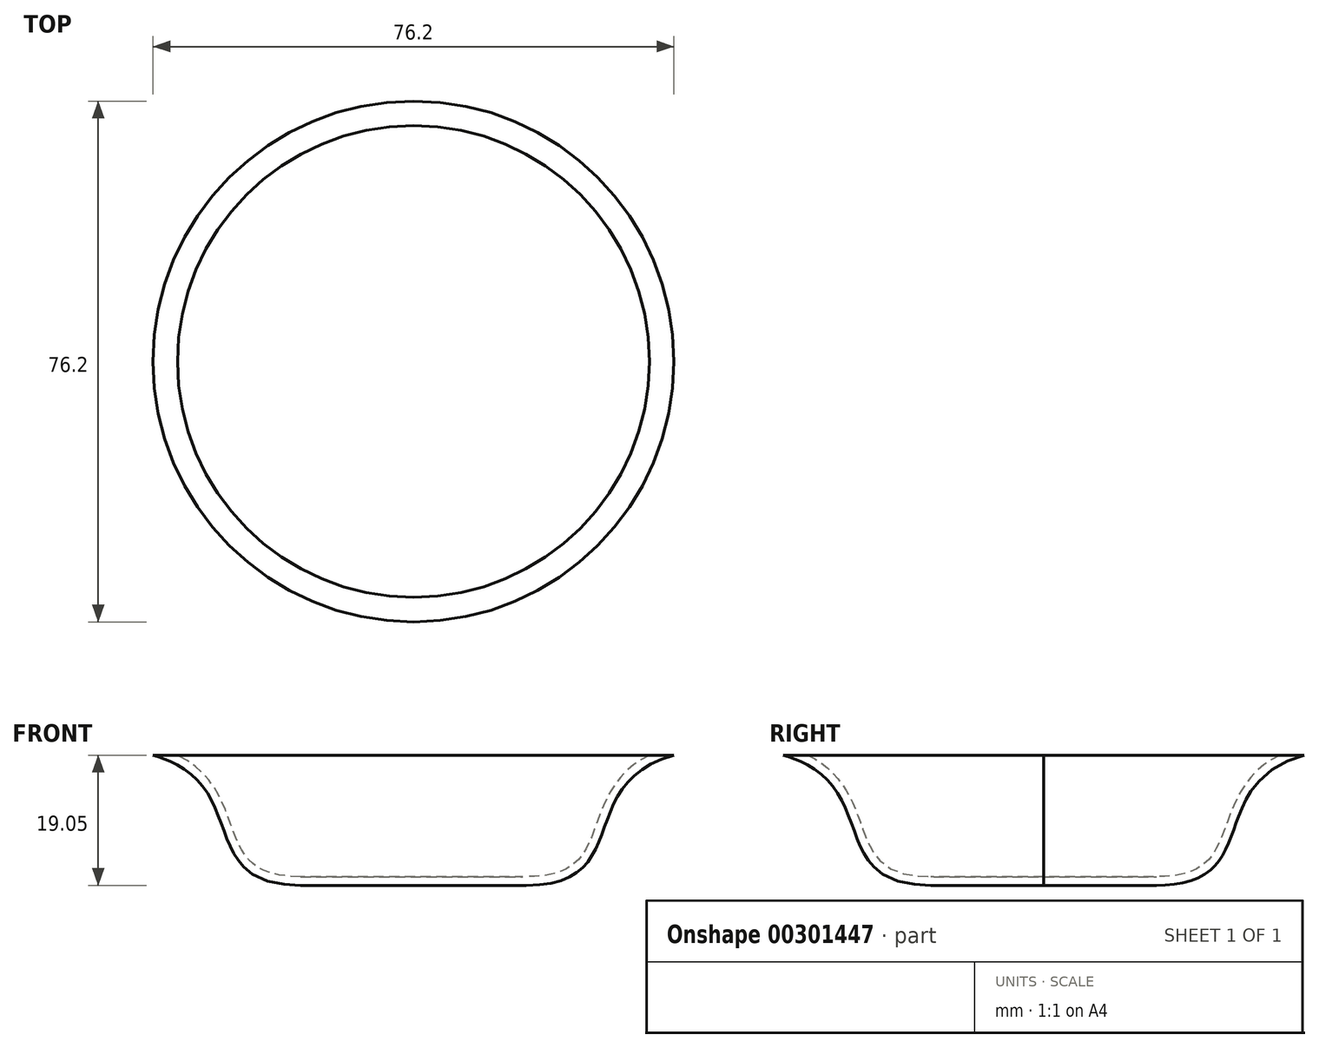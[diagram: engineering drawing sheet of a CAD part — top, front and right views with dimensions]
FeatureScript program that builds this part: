
annotation { "Feature Type Name" : "Feature", "Feature Type Description" : "" }
export const myFeature = defineFeature(function(context is Context, id is Id, definition is map)
    precondition{}
    {
        {
            var Q0;
            Q0=qCreatedBy(makeId("Front.planeOp"),FACE);
            var sketch = newSketch(context, id + "F0", { "sketchPlane" : qUnion([Q0])});
            skLineSegment(sketch, "E0", {"start": v(0, 0) * mm, "end": v(-16.51, 0) * mm});
            skLineSegment(sketch, "E1", {"start": v(-38.1, 19.05) * mm, "end": v(0, 19.05) * mm});
            skLineSegment(sketch, "E2", {"start": v(0, 19.05) * mm, "end": v(0, 0) * mm});
            skFitSpline(sketch, "E3", {"points": [v(-16.51, 0) * mm, v(-38.1, 19.05) * mm], "startDerivative": vector(-47.87, 0) * mm, "endDerivative": vector(-44.45, 12.45) * mm});
            skSolve(sketch);
        }
        {
            var Q0;
            Q0=makeQuery(id+"F0.imprint","IMPRINT",FACE,{"disambiguationData":[TD([[makeQuery(id+"F0.imprint","IMPRINT",EDGE,{"derivedFrom":sQuery(id+"F0.wireOp",EDGE,"E0")}),-1.0]])]});
            var Q1;
            Q1=sQuery(id+"F0.wireOp",EDGE,"E2");
            revolve(context, id + "F1", {"entities" : qUnion([Q0]), "axis" : qUnion([Q1]), "revolveType" : RevolveType.FULL});
        }
        {
            var Q0;
            Q0=makeQuery(id+"F1.opRevolve","SWEPT_FACE",FACE,{"disambiguationData":[OSD([sQuery(id+"F0.wireOp",EDGE,"E1")])]});
            shell(context, id + "F2", {"entities" : qUnion([Q0]), "thickness" : 1.27 * mm});
        }
    });
